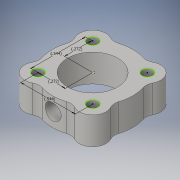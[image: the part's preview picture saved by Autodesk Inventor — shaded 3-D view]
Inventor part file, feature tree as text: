
AUTODESK INVENTOR PART (.ipt)
format: ipt  version: 2016 (Build 200138000, 138)  size: 164,864 bytes
history: native  units: in
note: dims shown in document units (in); Inventor stores cm internally (conversion verified against a paired STEP export)
features: sketch x1, fillet x1
ambient origin geometry x8: Origin, YZ Plane, XZ Plane, XY Plane, X Axis, Y Axis, Z Axis, Center Point
bodies: Solid1 (feature_tree)
feature tree (2):
  sketch  "Sketch1"  dims[d1=0.5445in d3=0.2722in d4=0.2722in]
  fillet  "Fillet1"  Radius=0.5445in
